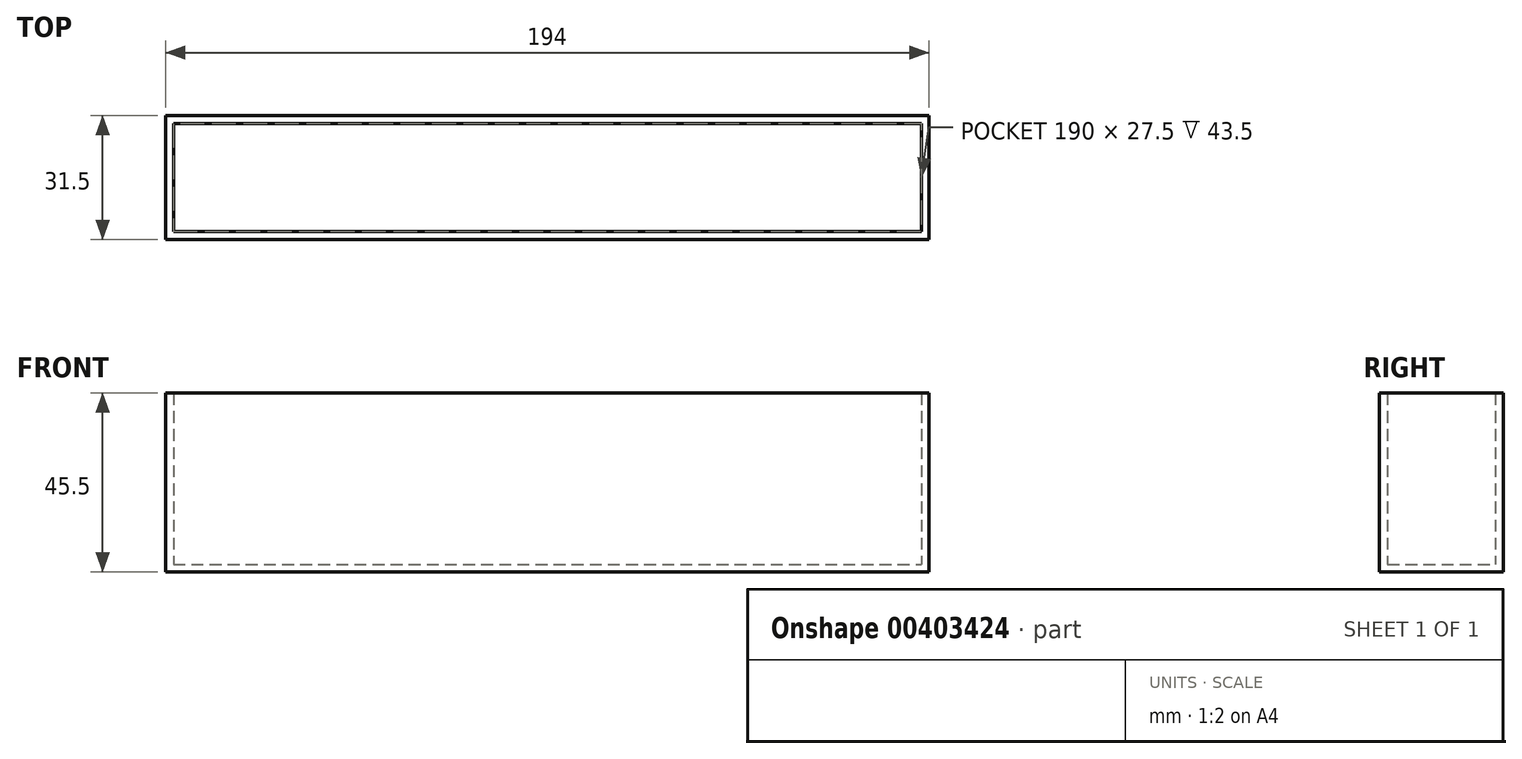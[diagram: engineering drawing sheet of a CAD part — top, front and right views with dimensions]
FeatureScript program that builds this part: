
annotation { "Feature Type Name" : "Feature", "Feature Type Description" : "" }
export const myFeature = defineFeature(function(context is Context, id is Id, definition is map)
    precondition{}
    {
        {
            var Q0;
            Q0=qCreatedBy(makeId("Front.planeOp"),FACE);
            var sketch = newSketch(context, id + "F0", { "sketchPlane" : qUnion([Q0])});
            skLineSegment(sketch, "E0.bottom", {"start": v(-89.8, 39.46) * mm, "end": v(100.2, 39.46) * mm});
            skLineSegment(sketch, "E0.top", {"start": v(-89.8, -4.04) * mm, "end": v(100.2, -4.04) * mm});
            skLineSegment(sketch, "E0.left", {"start": v(-89.8, 39.46) * mm, "end": v(-89.8, -4.04) * mm});
            skLineSegment(sketch, "E0.right", {"start": v(100.2, 39.46) * mm, "end": v(100.2, -4.04) * mm});
            skSolve(sketch);
        }
        {
            var Q0;
            Q0 = qSketchRegion(id + "F0", true);
            extrude(context, id + "F1", {"entities" : qUnion([Q0]), "endBound" : BoundingType.SYMMETRIC, "depth" : 27.5 * mm});
        }
        {
            var Q0;
            Q0=makeQuery(id+"F1.opExtrude","SWEPT_FACE",FACE,{"disambiguationData":[OSD([sQuery(id+"F0.wireOp",EDGE,"E0.bottom")])]});
            shell(context, id + "F2", {"entities" : qUnion([Q0]), "thickness" : 2 * mm, "oppositeDirection" : true});
        }
    });
